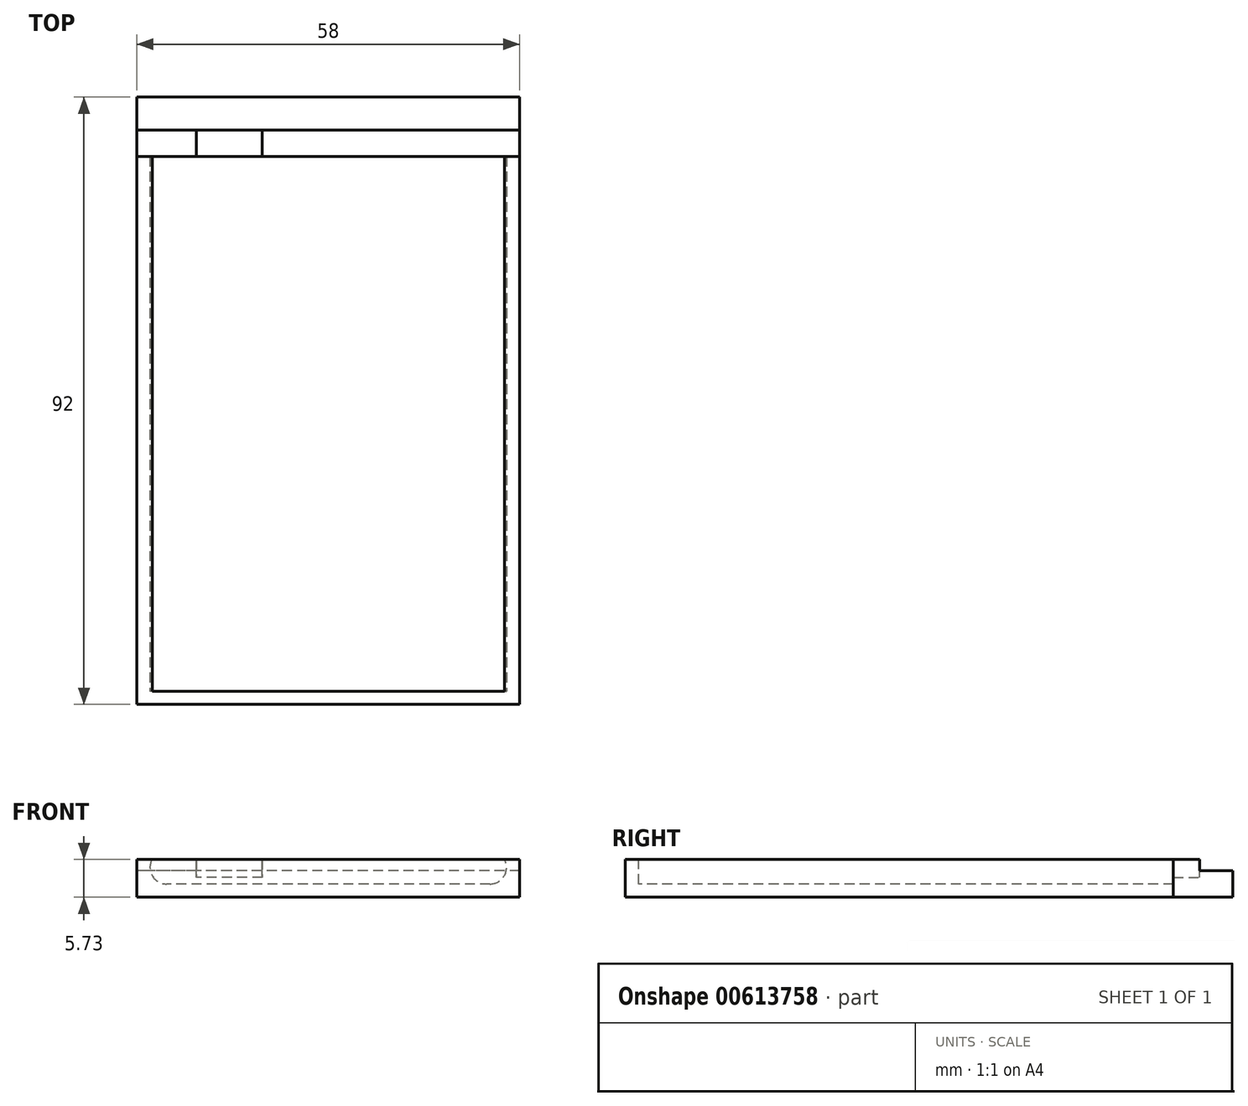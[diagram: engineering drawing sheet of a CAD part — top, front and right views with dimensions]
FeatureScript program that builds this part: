
annotation { "Feature Type Name" : "Feature", "Feature Type Description" : "" }
export const myFeature = defineFeature(function(context is Context, id is Id, definition is map)
    precondition{}
    {
        {
            var Q0;
            Q0=qCreatedBy(makeId("Top.planeOp"),FACE);
            var sketch = newSketch(context, id + "F0", { "sketchPlane" : qUnion([Q0])});
            skLineSegment(sketch, "E0.bottom", {"start": v(27, -38) * mm, "end": v(-27, -38) * mm});
            skLineSegment(sketch, "E0.top", {"start": v(27, 38) * mm, "end": v(-27, 38) * mm});
            skLineSegment(sketch, "E0.left", {"start": v(27, -38) * mm, "end": v(27, 38) * mm});
            skLineSegment(sketch, "E0.right", {"start": v(-27, -38) * mm, "end": v(-27, 38) * mm});
            skPoint(sketch, "E0.middle", {"position": v(0, 0) * mm});
            skLineSegment(sketch, "E1.0", {"start": v(-29, -40) * mm, "end": v(-29, 40) * mm});
            skLineSegment(sketch, "E1.1", {"start": v(29, -40) * mm, "end": v(-29, -40) * mm});
            skLineSegment(sketch, "E1.2", {"start": v(29, -40) * mm, "end": v(29, 40) * mm});
            skLineSegment(sketch, "E1.3", {"start": v(29, 40) * mm, "end": v(-29, 40) * mm});
            skSolve(sketch);
        }
        {
            var Q0;
            Q0 = qSketchRegion(id + "F0", true);
            var Q1;
            Q1=makeQuery(id+"F0.imprint","IMPRINT",FACE,{"disambiguationData":[TD([[makeQuery(id+"F0.imprint","IMPRINT",EDGE,{"derivedFrom":sQuery(id+"F0.wireOp",EDGE,"E0.bottom")}),-1.0]])]});
            extrude(context, id + "F1", {"entities" : qUnion([Q0, Q1]), "depth" : 9 * mm, "offsetDistance" : 25 * mm});
        }
        {
            var Q0;
            Q0=makeQuery(id+"F1.opExtrude","SWEPT_FACE",FACE,{"disambiguationData":[OSD([sQuery(id+"F0.wireOp",EDGE,"E1.1")])]});
            var sketch = newSketch(context, id + "F2", { "sketchPlane" : qUnion([Q0])});
            skLineSegment(sketch, "E2", {"start": v(-29, 4.5) * mm, "end": v(29, 4.5) * mm, "construction": true});
            skArc(sketch, "E3", {"start": v(-26.68, 5.73) * mm, "mid": v(-26.66, 3.24) * mm, "end": v(-24.5, 2) * mm});
            skArc(sketch, "E4", {"start": v(24.5, 2) * mm, "mid": v(26.66, 3.24) * mm, "end": v(26.68, 5.73) * mm});
            skLineSegment(sketch, "E5", {"start": v(24.5, 2) * mm, "end": v(-24.5, 2) * mm});
            skLineSegment(sketch, "E6", {"start": v(-29, 5.73) * mm, "end": v(29, 5.73) * mm});
            skPoint(sketch, "E7.start.orphan", {"position": v(-24.5, 7) * mm});
            skSolve(sketch);
        }
        {
            var Q0;
            Q0=makeQuery(id+"F2.imprint","IMPRINT",FACE,{"disambiguationData":[TD([[makeQuery(id+"F2.imprint","IMPRINT",EDGE,{"derivedFrom":sQuery(id+"F2.wireOp",EDGE,"E3")}),1.0]])]});
            var Q1;
            {var subQ0=sQuery(id+"F0.wireOp",EDGE,"E1.1");var subQ1=makeQuery(id+"F1.opExtrude","CAP_EDGE",EDGE,{"disambiguationData":[OSD([subQ0])],"isStart":false});Q1=makeQuery(id+"F2.imprint","IMPRINT",FACE,{"disambiguationData":[TD([[makeQuery(id+"F2.imprint","IMPRINT",EDGE,{"derivedFrom":subQ1}),1.0]])]});}
            extrude(context, id + "F3", {"entities" : qUnion([Q0, Q1]), "operationType" : NewBodyOperationType.REMOVE, "endBound" : BoundingType.THROUGH_ALL, "oppositeDirection" : true, "depth" : 25 * mm, "offsetDistance" : 25 * mm});
        }
        {
            var Q0;
            Q0=makeQuery(id+"F1.opExtrude","SWEPT_FACE",FACE,{"disambiguationData":[OSD([sQuery(id+"F0.wireOp",EDGE,"E1.1")])]});
            extrude(context, id + "F4", {"entities" : qUnion([Q0]), "operationType" : NewBodyOperationType.ADD, "depth" : 1 * mm, "offsetDistance" : 25 * mm});
        }
        {
            var Q0;
            Q0=makeQuery(id+"F4.opExtrude","CAP_FACE",FACE,{"disambiguationData":[OSD([sQuery(id+"F0.wireOp",EDGE,"E1.1")])],"isStart":false});
            var sketch = newSketch(context, id + "F5", { "sketchPlane" : qUnion([Q0])});
            skLineSegment(sketch, "E8.bottom", {"start": v(-29, 0) * mm, "end": v(29, 0) * mm});
            skLineSegment(sketch, "E8.top", {"start": v(-29, 5.73) * mm, "end": v(29, 5.73) * mm});
            skLineSegment(sketch, "E8.left", {"start": v(-29, 0) * mm, "end": v(-29, 5.73) * mm});
            skLineSegment(sketch, "E8.right", {"start": v(29, 0) * mm, "end": v(29, 5.73) * mm});
            skSolve(sketch);
        }
        {
            var Q0;
            {var subQ1=makeQuery(id+"F4.opExtrude","CAP_EDGE",EDGE,{"disambiguationData":[OSD([sQuery(id+"F2.wireOp",EDGE,"E3")])],"isStart":false});Q0=makeQuery(id+"F5.imprint","IMPRINT",FACE,{"disambiguationData":[TD([[makeQuery(id+"F5.imprint","IMPRINT",EDGE,{"derivedFrom":subQ1}),1.0]])]});}
            var Q1;
            Q1=makeQuery(id+"F5.imprint","IMPRINT",FACE,{"disambiguationData":[TD([[makeQuery(id+"F5.imprint","IMPRINT",EDGE,{"derivedFrom":sQuery(id+"F5.wireOp",EDGE,"E8.bottom")}),-1.0]])]});
            extrude(context, id + "F6", {"entities" : qUnion([Q0, Q1]), "operationType" : NewBodyOperationType.ADD, "depth" : 2 * mm, "offsetDistance" : 25 * mm});
        }
        {
            var Q0;
            Q0=makeQuery(id+"F1.opExtrude","SWEPT_FACE",FACE,{"disambiguationData":[OSD([sQuery(id+"F0.wireOp",EDGE,"E1.3")])]});
            var sketch = newSketch(context, id + "F7", { "sketchPlane" : qUnion([Q0])});
            skLineSegment(sketch, "E9.bottom", {"start": v(-29, 0) * mm, "end": v(29, 0) * mm});
            skLineSegment(sketch, "E9.top", {"start": v(-29, 2) * mm, "end": v(29, 2) * mm});
            skLineSegment(sketch, "E9.left", {"start": v(-29, 0) * mm, "end": v(-29, 2) * mm});
            skLineSegment(sketch, "E9.right", {"start": v(29, 0) * mm, "end": v(29, 2) * mm});
            skSolve(sketch);
        }
        {
            var Q0;
            Q0 = qSketchRegion(id + "F7", true);
            extrude(context, id + "F8", {"entities" : qUnion([Q0]), "depth" : 2 * mm, "offsetDistance" : 25 * mm});
        }
        {
            var Q0;
            Q0=makeQuery(id+"F8.opExtrude","SWEPT_FACE",FACE,{"disambiguationData":[OSD([sQuery(id+"F7.wireOp",EDGE,"E9.top")])]});
            var Q1;
            {var subQ0=sQuery(id+"F2.wireOp",EDGE,"E6");var subQ2=makeQuery(id+"F2.imprint","IMPRINT",EDGE,{"disambiguationData":[TD([[makeQuery(id+"F2.imprint","INTERSECT",VERTEX,{"derivedFrom":[sQuery(id+"F2.wireOp",EDGE,"E4"),subQ0]}),-1.0]])],"derivedFrom":subQ0});var subQ3=makeQuery(id+"F2.imprint","IMPRINT",EDGE,{"disambiguationData":[TD([[makeQuery(id+"F2.imprint","INTERSECT",VERTEX,{"derivedFrom":[sQuery(id+"F2.wireOp",EDGE,"E3"),subQ0]}),1.0]])],"derivedFrom":subQ0});Q1=makeQuery(id+"F6.boolean.opBoolean","MERGE",FACE,{"derivedFrom":[makeQuery(id+"F4.boolean.opBoolean","MERGE",FACE,{"derivedFrom":[makeQuery(id+"F3.boolean.opBoolean","COPY",FACE,{"derivedFrom":makeQuery(id+"F3.opExtrude","SWEPT_FACE",FACE,{"disambiguationData":[OSD([subQ0]),TDD([subQ3])]})}),makeQuery(id+"F4.opExtrude","SWEPT_FACE",FACE,{"disambiguationData":[OSD([subQ0]),TDD([makeQuery(id+"F3.boolean.opBoolean","COPY",EDGE,{"derivedFrom":makeQuery(id+"F3.opExtrude","CAP_EDGE",EDGE,{"disambiguationData":[OSD([subQ0]),TDD([subQ3])],"isStart":true})})])]})]}),makeQuery(id+"F4.boolean.opBoolean","MERGE",FACE,{"derivedFrom":[makeQuery(id+"F3.boolean.opBoolean","COPY",FACE,{"derivedFrom":makeQuery(id+"F3.opExtrude","SWEPT_FACE",FACE,{"disambiguationData":[OSD([subQ0]),TDD([subQ2])]})}),makeQuery(id+"F4.opExtrude","SWEPT_FACE",FACE,{"disambiguationData":[OSD([subQ0]),TDD([makeQuery(id+"F3.boolean.opBoolean","COPY",EDGE,{"derivedFrom":makeQuery(id+"F3.opExtrude","CAP_EDGE",EDGE,{"disambiguationData":[OSD([subQ0]),TDD([subQ2])],"isStart":true})})])]})]}),makeQuery(id+"F6.opExtrude","SWEPT_FACE",FACE,{"disambiguationData":[OSD([sQuery(id+"F5.wireOp",EDGE,"E8.top")])]})]});}
            extrude(context, id + "F9", {"entities" : qUnion([Q0]), "depth" : 1 * mm, "endBoundEntityFace" : qUnion([Q1]), "offsetDistance" : 25 * mm});
        }
        {
            var Q0;
            Q0=makeQuery(id+"F9.opExtrude","SWEPT_BODY",BODY,{"disambiguationData":[OSD([sQuery(id+"F7.wireOp",EDGE,"E9.top")])]});
            var Q1;
            Q1=makeQuery(id+"F8.opExtrude","SWEPT_BODY",BODY,{"disambiguationData":[OSD([sQuery(id+"F7.wireOp",EDGE,"E9.bottom"),sQuery(id+"F7.wireOp",EDGE,"E9.top"),sQuery(id+"F7.wireOp",EDGE,"E9.left"),sQuery(id+"F7.wireOp",EDGE,"E9.right")])]});
            booleanBodies(context, id + "F10", {"operationType" : BooleanOperationType.UNION, "tools" : qUnion([Q0, Q1])});
        }
        {
            var Q0;
            Q0=makeQuery(id+"F9.opExtrude","CAP_FACE",FACE,{"disambiguationData":[OSD([sQuery(id+"F7.wireOp",EDGE,"E9.top")])],"isStart":false});
            var Q1;
            {var subQ0=sQuery(id+"F2.wireOp",EDGE,"E6");var subQ2=makeQuery(id+"F2.imprint","IMPRINT",EDGE,{"disambiguationData":[TD([[makeQuery(id+"F2.imprint","INTERSECT",VERTEX,{"derivedFrom":[sQuery(id+"F2.wireOp",EDGE,"E4"),subQ0]}),-1.0]])],"derivedFrom":subQ0});var subQ3=makeQuery(id+"F2.imprint","IMPRINT",EDGE,{"disambiguationData":[TD([[makeQuery(id+"F2.imprint","INTERSECT",VERTEX,{"derivedFrom":[sQuery(id+"F2.wireOp",EDGE,"E3"),subQ0]}),1.0]])],"derivedFrom":subQ0});Q1=makeQuery(id+"F6.boolean.opBoolean","MERGE",FACE,{"derivedFrom":[makeQuery(id+"F4.boolean.opBoolean","MERGE",FACE,{"derivedFrom":[makeQuery(id+"F3.boolean.opBoolean","COPY",FACE,{"derivedFrom":makeQuery(id+"F3.opExtrude","SWEPT_FACE",FACE,{"disambiguationData":[OSD([subQ0]),TDD([subQ3])]})}),makeQuery(id+"F4.opExtrude","SWEPT_FACE",FACE,{"disambiguationData":[OSD([subQ0]),TDD([makeQuery(id+"F3.boolean.opBoolean","COPY",EDGE,{"derivedFrom":makeQuery(id+"F3.opExtrude","CAP_EDGE",EDGE,{"disambiguationData":[OSD([subQ0]),TDD([subQ3])],"isStart":true})})])]})]}),makeQuery(id+"F4.boolean.opBoolean","MERGE",FACE,{"derivedFrom":[makeQuery(id+"F3.boolean.opBoolean","COPY",FACE,{"derivedFrom":makeQuery(id+"F3.opExtrude","SWEPT_FACE",FACE,{"disambiguationData":[OSD([subQ0]),TDD([subQ2])]})}),makeQuery(id+"F4.opExtrude","SWEPT_FACE",FACE,{"disambiguationData":[OSD([subQ0]),TDD([makeQuery(id+"F3.boolean.opBoolean","COPY",EDGE,{"derivedFrom":makeQuery(id+"F3.opExtrude","CAP_EDGE",EDGE,{"disambiguationData":[OSD([subQ0]),TDD([subQ2])],"isStart":true})})])]})]}),makeQuery(id+"F6.opExtrude","SWEPT_FACE",FACE,{"disambiguationData":[OSD([sQuery(id+"F5.wireOp",EDGE,"E8.top")])]})]});}
            extrude(context, id + "F11", {"entities" : qUnion([Q0]), "endBound" : BoundingType.UP_TO_SURFACE, "depth" : 25 * mm, "endBoundEntityFace" : qUnion([Q1]), "offsetDistance" : 25 * mm});
        }
        {
            var Q0;
            {var subQ0=sQuery(id+"F7.wireOp",EDGE,"E9.top");Q0=makeQuery(id+"F11.opExtrude","SWEPT_FACE",FACE,{"disambiguationData":[OSD([subQ0]),TDD([makeQuery(id+"F9.opExtrude","CAP_EDGE",EDGE,{"disambiguationData":[OSD([subQ0]),TDD([makeQuery(id+"F8.opExtrude","CAP_EDGE",EDGE,{"disambiguationData":[OSD([subQ0])],"isStart":false})])],"isStart":false})])]});}
            var sketch = newSketch(context, id + "F12", { "sketchPlane" : qUnion([Q0])});
            skLineSegment(sketch, "E10", {"start": v(29, 4.37) * mm, "end": v(15, 4.37) * mm, "construction": true});
            skLineSegment(sketch, "E11.bottom", {"start": v(20, 5.73) * mm, "end": v(10, 5.73) * mm});
            skLineSegment(sketch, "E11.top", {"start": v(20, 3) * mm, "end": v(10, 3) * mm});
            skLineSegment(sketch, "E11.left", {"start": v(20, 5.73) * mm, "end": v(20, 3) * mm});
            skLineSegment(sketch, "E11.right", {"start": v(10, 5.73) * mm, "end": v(10, 3) * mm});
            skPoint(sketch, "E11.middle", {"position": v(15, 4.37) * mm});
            skSolve(sketch);
        }
        {
            var Q0;
            Q0=makeQuery(id+"F12.imprint","IMPRINT",FACE,{"disambiguationData":[TD([[makeQuery(id+"F12.imprint","IMPRINT",EDGE,{"derivedFrom":sQuery(id+"F12.wireOp",EDGE,"E11.bottom")}),1.0]])]});
            var Q1;
            {var subQ0=sQuery(id+"F7.wireOp",EDGE,"E9.top");Q1=makeQuery(id+"F11.opExtrude","SWEPT_FACE",FACE,{"disambiguationData":[OSD([subQ0]),TDD([makeQuery(id+"F9.opExtrude","CAP_EDGE",EDGE,{"disambiguationData":[OSD([subQ0]),TDD([makeQuery(id+"F8.opExtrude","CAP_EDGE",EDGE,{"disambiguationData":[OSD([subQ0])],"isStart":true})])],"isStart":false})])]});}
            extrude(context, id + "F13", {"entities" : qUnion([Q0]), "operationType" : NewBodyOperationType.REMOVE, "endBound" : BoundingType.UP_TO_SURFACE, "oppositeDirection" : true, "depth" : 25 * mm, "endBoundEntityFace" : qUnion([Q1]), "offsetDistance" : 25 * mm});
        }
        {
            var Q0;
            {var subQ0=sQuery(id+"F7.wireOp",EDGE,"E9.top");Q0=makeQuery(id+"F10.opBoolean","MERGE",FACE,{"derivedFrom":[makeQuery(id+"F8.opExtrude","CAP_FACE",FACE,{"disambiguationData":[OSD([sQuery(id+"F7.wireOp",EDGE,"E9.bottom"),subQ0,sQuery(id+"F7.wireOp",EDGE,"E9.left"),sQuery(id+"F7.wireOp",EDGE,"E9.right")])],"isStart":false}),makeQuery(id+"F9.opExtrude","SWEPT_FACE",FACE,{"disambiguationData":[OSD([subQ0]),TDD([makeQuery(id+"F8.opExtrude","CAP_EDGE",EDGE,{"disambiguationData":[OSD([subQ0])],"isStart":false})])]})]});}
            extrude(context, id + "F14", {"entities" : qUnion([Q0]), "operationType" : NewBodyOperationType.ADD, "depth" : 2 * mm, "offsetDistance" : 25 * mm});
        }
        {
            var Q0;
            Q0=makeQuery(id+"F14.opExtrude","CAP_FACE",FACE,{"disambiguationData":[OSD([sQuery(id+"F7.wireOp",EDGE,"E9.bottom"),sQuery(id+"F7.wireOp",EDGE,"E9.top"),sQuery(id+"F7.wireOp",EDGE,"E9.left"),sQuery(id+"F7.wireOp",EDGE,"E9.right")])],"isStart":false});
            extrude(context, id + "F15", {"entities" : qUnion([Q0]), "depth" : 5 * mm, "offsetDistance" : 25 * mm});
        }
        {
            var Q0;
            Q0=makeQuery(id+"F15.opExtrude","SWEPT_FACE",FACE,{"disambiguationData":[OSD([sQuery(id+"F7.wireOp",EDGE,"E9.top")])]});
            extrude(context, id + "F16", {"entities" : qUnion([Q0]), "operationType" : NewBodyOperationType.ADD, "depth" : 1 * mm, "offsetDistance" : 25 * mm});
        }
        {
            var Q0;
            {var subQ0=sQuery(id+"F7.wireOp",EDGE,"E9.top");Q0=makeQuery(id+"F13.boolean.opBoolean","SPLIT",FACE,{"disambiguationData":[TD([makeQuery(id+"F13.opExtrude","SWEPT_FACE",FACE,{"disambiguationData":[OSD([sQuery(id+"F12.wireOp",EDGE,"E11.left")])]})])],"derivedFrom":makeQuery(id+"F11.opExtrude","SWEPT_FACE",FACE,{"disambiguationData":[OSD([subQ0]),TDD([makeQuery(id+"F9.opExtrude","CAP_EDGE",EDGE,{"disambiguationData":[OSD([subQ0]),TDD([makeQuery(id+"F8.opExtrude","CAP_EDGE",EDGE,{"disambiguationData":[OSD([subQ0])],"isStart":false})])],"isStart":false})])]})});}
            var Q1;
            {var subQ0=sQuery(id+"F7.wireOp",EDGE,"E9.top");Q1=makeQuery(id+"F13.boolean.opBoolean","SPLIT",FACE,{"disambiguationData":[TD([makeQuery(id+"F13.opExtrude","SWEPT_FACE",FACE,{"disambiguationData":[OSD([sQuery(id+"F12.wireOp",EDGE,"E11.right")])]})])],"derivedFrom":makeQuery(id+"F11.opExtrude","SWEPT_FACE",FACE,{"disambiguationData":[OSD([subQ0]),TDD([makeQuery(id+"F9.opExtrude","CAP_EDGE",EDGE,{"disambiguationData":[OSD([subQ0]),TDD([makeQuery(id+"F8.opExtrude","CAP_EDGE",EDGE,{"disambiguationData":[OSD([subQ0])],"isStart":false})])],"isStart":false})])]})});}
            var Q2;
            {var subQ0=sQuery(id+"F7.wireOp",EDGE,"E9.top");Q2=makeQuery(id+"F16.boolean.opBoolean","MERGE",FACE,{"derivedFrom":[makeQuery(id+"F15.opExtrude","CAP_FACE",FACE,{"disambiguationData":[OSD([sQuery(id+"F7.wireOp",EDGE,"E9.bottom"),subQ0,sQuery(id+"F7.wireOp",EDGE,"E9.left"),sQuery(id+"F7.wireOp",EDGE,"E9.right")])],"isStart":true}),makeQuery(id+"F16.opExtrude","SWEPT_FACE",FACE,{"disambiguationData":[OSD([subQ0]),TDD([makeQuery(id+"F15.opExtrude","CAP_EDGE",EDGE,{"disambiguationData":[OSD([subQ0])],"isStart":true})])]})]});}
            extrude(context, id + "F17", {"entities" : qUnion([Q0, Q1]), "operationType" : NewBodyOperationType.ADD, "endBound" : BoundingType.UP_TO_SURFACE, "depth" : 25 * mm, "endBoundEntityFace" : qUnion([Q2]), "offsetDistance" : 25 * mm});
        }
    });
